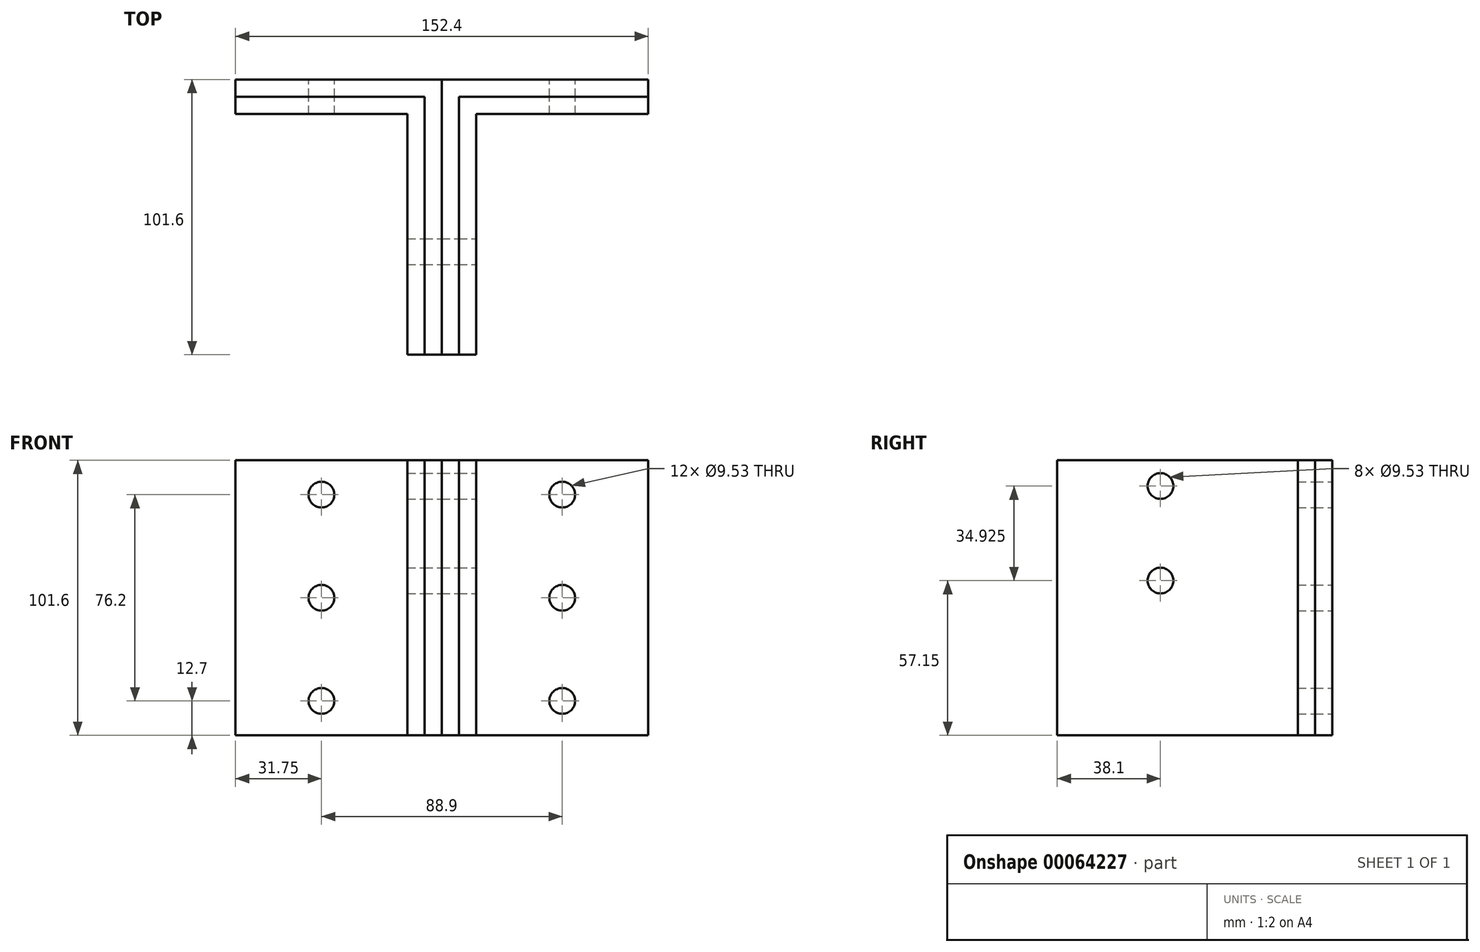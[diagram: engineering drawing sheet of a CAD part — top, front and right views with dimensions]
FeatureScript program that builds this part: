
annotation { "Feature Type Name" : "Feature", "Feature Type Description" : "" }
export const myFeature = defineFeature(function(context is Context, id is Id, definition is map)
    precondition{}
    {
        {
            var Q0;
            Q0=qCreatedBy(makeId("Top.planeOp"),FACE);
            var sketch = newSketch(context, id + "F0", { "sketchPlane" : qUnion([Q0])});
            skLineSegment(sketch, "E0", {"start": v(0, 0) * mm, "end": v(0, -101.6) * mm});
            skLineSegment(sketch, "E1", {"start": v(0, -101.6) * mm, "end": v(6.35, -101.6) * mm});
            skLineSegment(sketch, "E2", {"start": v(6.35, -101.6) * mm, "end": v(6.35, -6.35) * mm});
            skLineSegment(sketch, "E3", {"start": v(6.35, -6.35) * mm, "end": v(76.2, -6.35) * mm});
            skLineSegment(sketch, "E4", {"start": v(76.2, -6.35) * mm, "end": v(76.2, 0) * mm});
            skLineSegment(sketch, "E5", {"start": v(76.2, 0) * mm, "end": v(0, 0) * mm});
            skSolve(sketch);
        }
        {
            var Q0;
            Q0 = qSketchRegion(id + "F0", true);
            extrude(context, id + "F1", {"entities" : qUnion([Q0]), "endBound" : BoundingType.SYMMETRIC, "depth" : 101.6 * mm});
        }
        {
            var Q0;
            Q0=qCreatedBy(makeId("Top.planeOp"),FACE);
            var sketch = newSketch(context, id + "F2", { "sketchPlane" : qUnion([Q0])});
            skLineSegment(sketch, "E6", {"start": v(0, 0) * mm, "end": v(-76.2, 0) * mm});
            skLineSegment(sketch, "E7", {"start": v(-76.2, 0) * mm, "end": v(-76.2, -6.35) * mm});
            skLineSegment(sketch, "E8", {"start": v(-76.2, -6.35) * mm, "end": v(-6.35, -6.35) * mm});
            skLineSegment(sketch, "E9", {"start": v(-6.35, -6.35) * mm, "end": v(-6.35, -101.6) * mm});
            skLineSegment(sketch, "E10", {"start": v(-6.35, -101.6) * mm, "end": v(0, -101.6) * mm});
            skLineSegment(sketch, "E11", {"start": v(0, 0) * mm, "end": v(0, -101.6) * mm});
            skSolve(sketch);
        }
        {
            var Q0;
            Q0 = qSketchRegion(id + "F2", true);
            extrude(context, id + "F3", {"entities" : qUnion([Q0]), "endBound" : BoundingType.SYMMETRIC, "depth" : 101.6 * mm});
        }
        {
            var Q0;
            Q0=qCreatedBy(makeId("Top.planeOp"),FACE);
            var sketch = newSketch(context, id + "F4", { "sketchPlane" : qUnion([Q0])});
            skLineSegment(sketch, "E12", {"start": v(-6.35, -6.35) * mm, "end": v(-6.35, -101.6) * mm});
            skLineSegment(sketch, "E13", {"start": v(-6.35, -101.6) * mm, "end": v(-12.7, -101.6) * mm});
            skLineSegment(sketch, "E14", {"start": v(-12.7, -101.6) * mm, "end": v(-12.7, -12.7) * mm});
            skLineSegment(sketch, "E15", {"start": v(-12.7, -12.7) * mm, "end": v(-76.2, -12.7) * mm});
            skLineSegment(sketch, "E16", {"start": v(-76.2, -12.7) * mm, "end": v(-76.2, -6.35) * mm});
            skLineSegment(sketch, "E17", {"start": v(-76.2, -6.35) * mm, "end": v(-6.35, -6.35) * mm});
            skLineSegment(sketch, "E18.MirrorCS", {"start": v(6.35, -101.6) * mm, "end": v(12.7, -101.6) * mm});
            skLineSegment(sketch, "E19.MirrorCS", {"start": v(6.35, -6.35) * mm, "end": v(6.35, -101.6) * mm});
            skLineSegment(sketch, "E20.MirrorCS", {"start": v(12.7, -101.6) * mm, "end": v(12.7, -12.7) * mm});
            skLineSegment(sketch, "E21.MirrorCS", {"start": v(76.2, -12.7) * mm, "end": v(76.2, -6.35) * mm});
            skLineSegment(sketch, "E22.MirrorCS", {"start": v(76.2, -6.35) * mm, "end": v(6.35, -6.35) * mm});
            skLineSegment(sketch, "E23.MirrorCS", {"start": v(12.7, -12.7) * mm, "end": v(76.2, -12.7) * mm});
            skSolve(sketch);
        }
        {
            var Q0;
            Q0 = qSketchRegion(id + "F4", true);
            extrude(context, id + "F5", {"entities" : qUnion([Q0]), "endBound" : BoundingType.SYMMETRIC, "depth" : 101.6 * mm});
        }
        {
            var Q0;
            Q0=qCreatedBy(makeId("Front.planeOp"),FACE);
            var sketch = newSketch(context, id + "F6", { "sketchPlane" : qUnion([Q0])});
            skCircle(sketch, "E24", {"center": v(44.45, 38.1) * mm, "radius": 4.76 * mm});
            skCircle(sketch, "E25.0.1.0", {"center": v(44.45, 0) * mm, "radius": 4.76 * mm});
            skCircle(sketch, "E25.0.2.0", {"center": v(44.45, -38.1) * mm, "radius": 4.76 * mm});
            skCircle(sketch, "E25.1.0.0", {"center": v(-44.45, 38.1) * mm, "radius": 4.76 * mm});
            skCircle(sketch, "E25.1.1.0", {"center": v(-44.45, 0) * mm, "radius": 4.76 * mm});
            skCircle(sketch, "E25.1.2.0", {"center": v(-44.45, -38.1) * mm, "radius": 4.76 * mm});
            skLineSegment(sketch, "E25.direction1", {"start": v(44.45, 38.1) * mm, "end": v(-44.45, 38.1) * mm, "construction": true});
            skLineSegment(sketch, "E25.direction2", {"start": v(44.45, 38.1) * mm, "end": v(44.45, 0) * mm, "construction": true});
            skSolve(sketch);
        }
        {
            var Q0;
            Q0 = qSketchRegion(id + "F6", true);
            extrude(context, id + "F7", {"entities" : qUnion([Q0]), "operationType" : NewBodyOperationType.REMOVE, "endBound" : BoundingType.THROUGH_ALL, "depth" : 25.4 * mm});
        }
        {
            var Q0;
            Q0=makeQuery(id+"F5.opExtrude","SWEPT_FACE",FACE,{"disambiguationData":[OSD([sQuery(id+"F4.wireOp",EDGE,"E20.MirrorCS")])]});
            var sketch = newSketch(context, id + "F8", { "sketchPlane" : qUnion([Q0])});
            skCircle(sketch, "E26", {"center": v(-63.5, 41.28) * mm, "radius": 4.76 * mm});
            skCircle(sketch, "E27.0.1.0", {"center": v(-63.5, 6.35) * mm, "radius": 4.76 * mm});
            skLineSegment(sketch, "E27.direction1", {"start": v(-63.5, 41.28) * mm, "end": v(-31.75, 41.28) * mm, "construction": true});
            skLineSegment(sketch, "E27.direction2", {"start": v(-63.5, 41.28) * mm, "end": v(-63.5, 6.35) * mm, "construction": true});
            skSolve(sketch);
        }
        {
            var Q0;
            Q0 = qSketchRegion(id + "F8", true);
            extrude(context, id + "F9", {"entities" : qUnion([Q0]), "operationType" : NewBodyOperationType.REMOVE, "endBound" : BoundingType.THROUGH_ALL, "oppositeDirection" : true, "depth" : 25.4 * mm});
        }
    });
